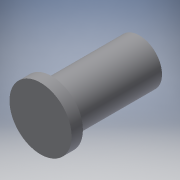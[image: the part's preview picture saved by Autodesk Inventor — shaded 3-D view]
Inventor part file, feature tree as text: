
AUTODESK INVENTOR PART (.ipt)
format: ipt  version: 2016 (Build 200138000, 138)  size: 102,400 bytes
history: native  units: in
note: dims shown in document units (in); Inventor stores cm internally (conversion verified against a paired STEP export)
features: extrude x2, sketch x2, reference x2
ambient origin geometry x8: Origin, YZ Plane, XZ Plane, XY Plane, X Axis, Y Axis, Z Axis, Center Point
bodies: Solid1 (feature_tree)
feature tree (6):
  extrude  "Extrusion1"  Depth=0.3051in TaperAngle=0.0deg
  extrude  "Extrusion2"  Depth=0.0394in TaperAngle=0.0deg
  sketch  "Sketch1"  dims[d0=0.1575in d1=0.3051in d2=0.0in]
  reference  "Reference1"
  reference  "Reference2"
  sketch  "Sketch2"  dims[d3=0.2165in d4=0.0394in d5=0.0in]
